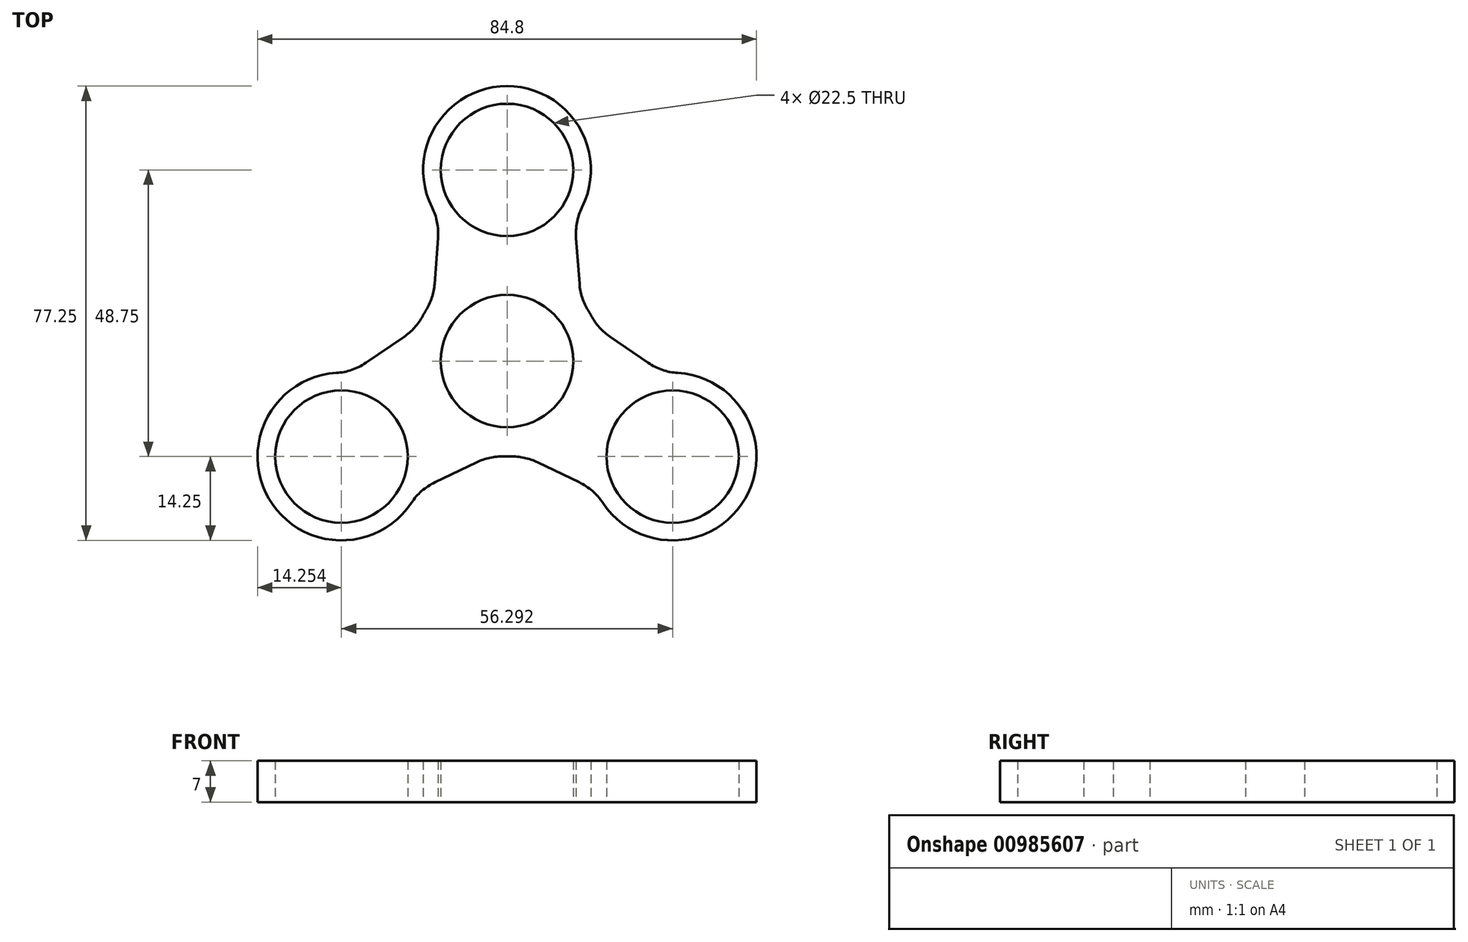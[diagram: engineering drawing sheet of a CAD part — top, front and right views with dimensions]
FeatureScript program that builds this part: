
annotation { "Feature Type Name" : "Feature", "Feature Type Description" : "" }
export const myFeature = defineFeature(function(context is Context, id is Id, definition is map)
    precondition{}
    {
        {
            var Q0;
            Q0=qCreatedBy(makeId("Top.planeOp"),FACE);
            var sketch = newSketch(context, id + "F0", { "sketchPlane" : qUnion([Q0])});
            skCircle(sketch, "E0", {"center": v(0, 0) * mm, "radius": 11.25 * mm});
            skCircle(sketch, "E1", {"center": v(0, 0) * mm, "radius": 16.25 * mm});
            skCircle(sketch, "E2", {"center": v(0, 32.5) * mm, "radius": 11.25 * mm});
            skCircle(sketch, "E3", {"center": v(0, 32.5) * mm, "radius": 14.25 * mm});
            skLineSegment(sketch, "E4", {"start": v(11.49, 24.07) * mm, "end": v(12.52, 10.36) * mm});
            skLineSegment(sketch, "E5.MirrorCS", {"start": v(-11.49, 24.07) * mm, "end": v(-12.52, 10.36) * mm});
            skLineSegment(sketch, "E6.1.0", {"start": v(-26.6, -2.09) * mm, "end": v(-15.23, 5.66) * mm});
            skCircle(sketch, "E6.1.1", {"center": v(-28.15, -16.25) * mm, "radius": 14.25 * mm});
            skCircle(sketch, "E6.1.2", {"center": v(-28.15, -16.25) * mm, "radius": 11.25 * mm});
            skLineSegment(sketch, "E6.1.3", {"start": v(-15.1, -21.99) * mm, "end": v(-2.71, -16.02) * mm});
            skLineSegment(sketch, "E6.2.0", {"start": v(15.1, -21.99) * mm, "end": v(2.71, -16.02) * mm});
            skCircle(sketch, "E6.2.1", {"center": v(28.15, -16.25) * mm, "radius": 14.25 * mm});
            skCircle(sketch, "E6.2.2", {"center": v(28.15, -16.25) * mm, "radius": 11.25 * mm});
            skLineSegment(sketch, "E6.2.3", {"start": v(26.6, -2.09) * mm, "end": v(15.23, 5.66) * mm});
            skSolve(sketch);
        }
        {
            var Q0;
            {var subQ6=sQuery(id+"F0.wireOp",EDGE,"E1");var subQ9=sQuery(id+"F0.wireOp",EDGE,"6e165e5a-116d-4390-8e23-ed30580c4e440.MirrorCS");var subQ10=makeQuery(id+"F0.imprint","INTERSECT",VERTEX,{"derivedFrom":[subQ6,subQ9]});Q0=makeQuery(id+"F0.imprint","IMPRINT",FACE,{"disambiguationData":[TD([[makeQuery(id+"F0.imprint","IMPRINT",EDGE,{"disambiguationData":[TD([[subQ10,-1.0]])],"derivedFrom":subQ6}),-1.0]])]});}
            var Q1;
            Q1=makeQuery(id+"F0.imprint","IMPRINT",FACE,{"disambiguationData":[TD([[makeQuery(id+"F0.imprint","IMPRINT",EDGE,{"derivedFrom":sQuery(id+"F0.wireOp",EDGE,"8341431b-4db8-486c-b9f8-18b4c291cda5.1.1")}),-1.0]])]});
            var Q2;
            Q2=makeQuery(id+"F0.imprint","IMPRINT",FACE,{"disambiguationData":[TD([[makeQuery(id+"F0.imprint","IMPRINT",EDGE,{"derivedFrom":sQuery(id+"F0.wireOp",EDGE,"E0")}),-1.0]])]});
            var Q3;
            {var subQ1=sQuery(id+"F0.wireOp",EDGE,"E1");var subQ9=sQuery(id+"F0.wireOp",EDGE,"E4");var subQ10=makeQuery(id+"F0.imprint","INTERSECT",VERTEX,{"derivedFrom":[subQ1,subQ9]});Q3=makeQuery(id+"F0.imprint","IMPRINT",FACE,{"disambiguationData":[TD([[makeQuery(id+"F0.imprint","IMPRINT",EDGE,{"disambiguationData":[TD([[subQ10,1.0]])],"derivedFrom":subQ1}),-1.0]])]});}
            var Q4;
            Q4=makeQuery(id+"F0.imprint","IMPRINT",FACE,{"disambiguationData":[TD([[makeQuery(id+"F0.imprint","IMPRINT",EDGE,{"derivedFrom":sQuery(id+"F0.wireOp",EDGE,"8341431b-4db8-486c-b9f8-18b4c291cda5.2.1")}),-1.0]])]});
            var Q5;
            {var subQ5=sQuery(id+"F0.wireOp",EDGE,"GQXUVbkL-2V5v-3tlb-Pwkm-8WP8JiNHhsI3");Q5=makeQuery(id+"F0.imprint","IMPRINT",FACE,{"disambiguationData":[TD([[makeQuery(id+"F0.imprint","IMPRINT",EDGE,{"derivedFrom":subQ5}),-1.0]])]});}
            var Q6;
            {var subQ5=sQuery(id+"F0.wireOp",EDGE,"GQXUVbkL-2V5v-3tlb-Pwkm-8WP8JiNHhsI3");Q6=makeQuery(id+"F0.imprint","IMPRINT",FACE,{"disambiguationData":[TD([[makeQuery(id+"F0.imprint","IMPRINT",EDGE,{"derivedFrom":subQ5}),1.0]])]});}
            var Q7;
            Q7=makeQuery(id+"F0.imprint","IMPRINT",FACE,{"disambiguationData":[TD([[makeQuery(id+"F0.imprint","IMPRINT",EDGE,{"derivedFrom":sQuery(id+"F0.wireOp",EDGE,"E2")}),-1.0]])]});
            var Q8;
            Q8=makeQuery(id+"F0.imprint","IMPRINT",FACE,{"disambiguationData":[TD([[makeQuery(id+"F0.imprint","IMPRINT",EDGE,{"derivedFrom":sQuery(id+"F0.wireOp",EDGE,"E6.1.2")}),-1.0]])]});
            var Q9;
            Q9=makeQuery(id+"F0.imprint","IMPRINT",FACE,{"disambiguationData":[TD([[makeQuery(id+"F0.imprint","IMPRINT",EDGE,{"derivedFrom":sQuery(id+"F0.wireOp",EDGE,"E6.2.2")}),-1.0]])]});
            extrude(context, id + "F1", {"entities" : qUnion([Q0, Q1, Q2, Q3, Q4, Q5, Q6, Q7, Q8, Q9]), "depth" : 7 * mm, "offsetDistance" : 25 * mm});
        }
        {
            var Q0;
            Q0=makeQuery(id+"F1.opExtrude","SWEPT_EDGE",EDGE,{"disambiguationData":[OSD([sQuery(id+"F0.wireOp",EDGE,"E3"),sQuery(id+"F0.wireOp",EDGE,"E5.MirrorCS")])]});
            var Q1;
            Q1=makeQuery(id+"F1.opExtrude","SWEPT_EDGE",EDGE,{"disambiguationData":[OSD([sQuery(id+"F0.wireOp",EDGE,"E1"),sQuery(id+"F0.wireOp",EDGE,"E5.MirrorCS")])]});
            var Q2;
            Q2=makeQuery(id+"F1.opExtrude","SWEPT_EDGE",EDGE,{"disambiguationData":[OSD([sQuery(id+"F0.wireOp",EDGE,"E1"),sQuery(id+"F0.wireOp",EDGE,"E6.1.0")])]});
            var Q3;
            Q3=makeQuery(id+"F1.opExtrude","SWEPT_EDGE",EDGE,{"disambiguationData":[OSD([sQuery(id+"F0.wireOp",EDGE,"E6.1.0"),sQuery(id+"F0.wireOp",EDGE,"E6.1.1")])]});
            var Q4;
            Q4=makeQuery(id+"F1.opExtrude","SWEPT_EDGE",EDGE,{"disambiguationData":[OSD([sQuery(id+"F0.wireOp",EDGE,"E1"),sQuery(id+"F0.wireOp",EDGE,"E6.2.0")])]});
            var Q5;
            Q5=makeQuery(id+"F1.opExtrude","SWEPT_EDGE",EDGE,{"disambiguationData":[OSD([sQuery(id+"F0.wireOp",EDGE,"E1"),sQuery(id+"F0.wireOp",EDGE,"E6.1.3")])]});
            var Q6;
            Q6=makeQuery(id+"F1.opExtrude","SWEPT_EDGE",EDGE,{"disambiguationData":[OSD([sQuery(id+"F0.wireOp",EDGE,"E6.2.0"),sQuery(id+"F0.wireOp",EDGE,"E6.2.1")])]});
            var Q7;
            Q7=makeQuery(id+"F1.opExtrude","SWEPT_EDGE",EDGE,{"disambiguationData":[OSD([sQuery(id+"F0.wireOp",EDGE,"E6.1.1"),sQuery(id+"F0.wireOp",EDGE,"E6.1.3")])]});
            var Q8;
            Q8=makeQuery(id+"F1.opExtrude","SWEPT_EDGE",EDGE,{"disambiguationData":[OSD([sQuery(id+"F0.wireOp",EDGE,"E6.2.1"),sQuery(id+"F0.wireOp",EDGE,"E6.2.3")])]});
            var Q9;
            Q9=makeQuery(id+"F1.opExtrude","SWEPT_EDGE",EDGE,{"disambiguationData":[OSD([sQuery(id+"F0.wireOp",EDGE,"E1"),sQuery(id+"F0.wireOp",EDGE,"E6.2.3")])]});
            var Q10;
            Q10=makeQuery(id+"F1.opExtrude","SWEPT_EDGE",EDGE,{"disambiguationData":[OSD([sQuery(id+"F0.wireOp",EDGE,"E1"),sQuery(id+"F0.wireOp",EDGE,"E4")])]});
            var Q11;
            Q11=makeQuery(id+"F1.opExtrude","SWEPT_EDGE",EDGE,{"disambiguationData":[OSD([sQuery(id+"F0.wireOp",EDGE,"E3"),sQuery(id+"F0.wireOp",EDGE,"E4")])]});
            fillet(context, id + "F2", {"entities" : qUnion([Q0, Q1, Q2, Q3, Q4, Q5, Q6, Q7, Q8, Q9, Q10, Q11]), "radius" : 10 * mm, "tangentPropagation" : true, "allowEdgeOverflow" : false});
        }
    });
